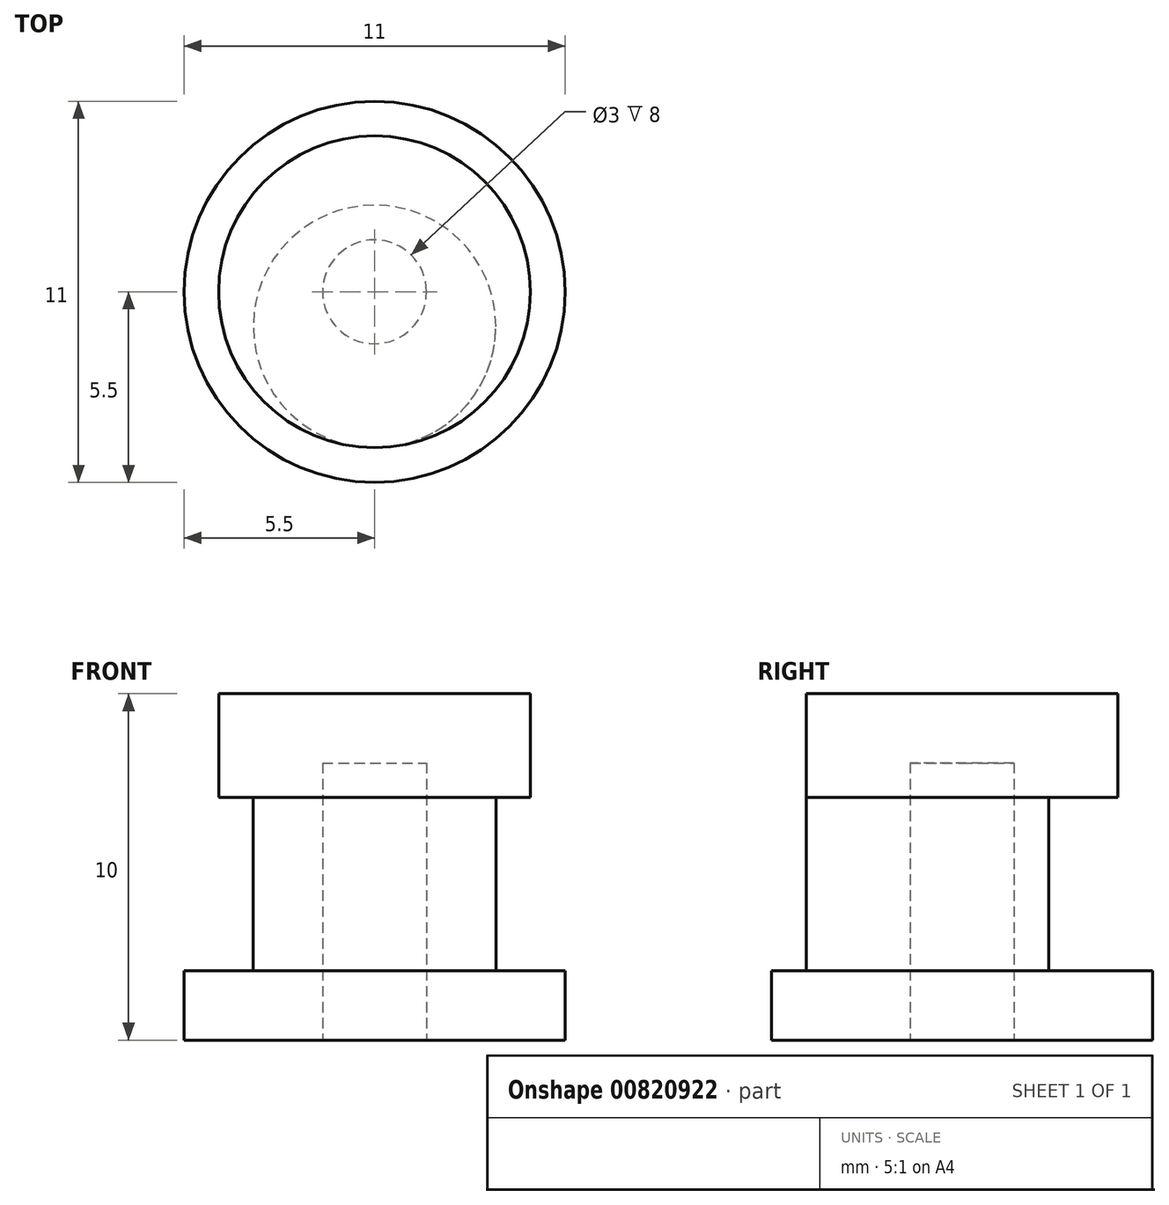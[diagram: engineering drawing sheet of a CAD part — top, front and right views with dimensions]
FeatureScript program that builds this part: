
annotation { "Feature Type Name" : "Feature", "Feature Type Description" : "" }
export const myFeature = defineFeature(function(context is Context, id is Id, definition is map)
    precondition{}
    {
        {
            var Q0;
            Q0=qCreatedBy(makeId("Top.planeOp"),FACE);
            var sketch = newSketch(context, id + "F0", { "sketchPlane" : qUnion([Q0])});
            skCircle(sketch, "E0", {"center": v(0, 0) * mm, "radius": 5.5 * mm});
            skSolve(sketch);
        }
        {
            var Q0;
            Q0=makeQuery(id+"F0.imprint","IMPRINT",FACE,{"disambiguationData":[TD([[makeQuery(id+"F0.imprint","IMPRINT",EDGE,{"derivedFrom":sQuery(id+"F0.wireOp",EDGE,"E0")}),1.0]])]});
            extrude(context, id + "F1", {"entities" : qUnion([Q0]), "depth" : 2 * mm, "offsetDistance" : 25 * mm});
        }
        {
            var Q0;
            Q0=makeQuery(id+"F1.opExtrude","CAP_FACE",FACE,{"disambiguationData":[OSD([sQuery(id+"F0.wireOp",EDGE,"E0")])],"isStart":false});
            var sketch = newSketch(context, id + "F2", { "sketchPlane" : qUnion([Q0])});
            skCircle(sketch, "E1", {"center": v(0, -1) * mm, "radius": 3.5 * mm});
            skSolve(sketch);
        }
        {
            var Q0;
            Q0=makeQuery(id+"F2.imprint","IMPRINT",FACE,{"disambiguationData":[TD([[makeQuery(id+"F2.imprint","IMPRINT",EDGE,{"derivedFrom":sQuery(id+"F2.wireOp",EDGE,"E1")}),1.0]])]});
            extrude(context, id + "F3", {"entities" : qUnion([Q0]), "operationType" : NewBodyOperationType.ADD, "depth" : 5 * mm, "offsetDistance" : 25 * mm});
        }
        {
            var Q0;
            Q0=makeQuery(id+"F3.opExtrude","CAP_FACE",FACE,{"disambiguationData":[OSD([sQuery(id+"F2.wireOp",EDGE,"E1")])],"isStart":false});
            var sketch = newSketch(context, id + "F4", { "sketchPlane" : qUnion([Q0])});
            skCircle(sketch, "E2", {"center": v(0, 0) * mm, "radius": 4.5 * mm});
            skSolve(sketch);
        }
        {
            var Q0;
            Q0 = qSketchRegion(id + "F4", true);
            extrude(context, id + "F5", {"entities" : qUnion([Q0]), "operationType" : NewBodyOperationType.ADD, "depth" : 3 * mm, "offsetDistance" : 25 * mm});
        }
        {
            var Q0;
            Q0=makeQuery(id+"F1.opExtrude","CAP_FACE",FACE,{"disambiguationData":[OSD([sQuery(id+"F0.wireOp",EDGE,"E0")])],"isStart":true});
            var sketch = newSketch(context, id + "F6", { "sketchPlane" : qUnion([Q0])});
            skCircle(sketch, "E3", {"center": v(0, 0) * mm, "radius": 1.5 * mm});
            skSolve(sketch);
        }
        {
            var Q0;
            Q0=makeQuery(id+"F6.imprint","IMPRINT",FACE,{"disambiguationData":[TD([[makeQuery(id+"F6.imprint","IMPRINT",EDGE,{"derivedFrom":sQuery(id+"F6.wireOp",EDGE,"E3")}),1.0]])]});
            extrude(context, id + "F7", {"entities" : qUnion([Q0]), "operationType" : NewBodyOperationType.REMOVE, "oppositeDirection" : true, "depth" : 8 * mm, "offsetDistance" : 25 * mm});
        }
    });
